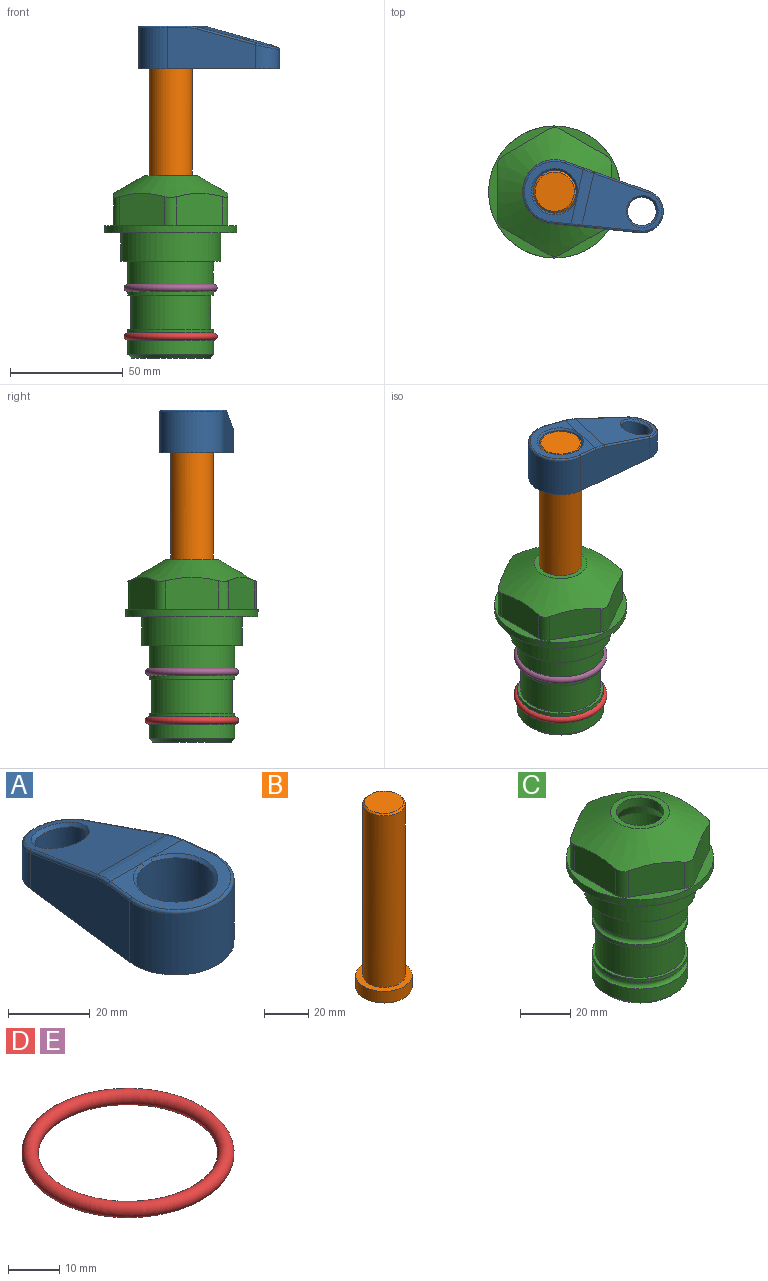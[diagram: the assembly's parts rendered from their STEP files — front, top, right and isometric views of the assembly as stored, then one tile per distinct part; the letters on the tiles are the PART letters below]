
ASSEMBLY  parts=5 mates=4
PART A: 31 faces, bbox 31.7x65.5x19.8 mm
  f0: plane 39.12x18.26mm, normal (0.99,0.12,0), area 612.2mm2, adj f1,f4,f7,f11,f13,f15
  f1: cylinder r=9.53mm len=18.91mm, axis (0,0,-1), area 296.1mm2, adj f0,f2,f7,f17
  f2: plane 39.12x18.26mm, normal (-0.99,0.12,0), area 612.2mm2, adj f1,f4,f7,f12,f14,f16
  f3: cylinder r=6.35mm len=12.7mm, axis (0,0,-1), area 362.4mm2, adj f7,f18
  f4: cylinder r=14.29mm len=28.58mm, axis (0,0,-1), area 882.2mm2, adj f0,f2,f7,f10
  f5: cylinder r=9.53mm len=19.05mm, axis (0,0,-1), area 1092.6mm2, adj f7,f19,f20
  f6: plane 26.99x23.69mm, normal (0,0,1), area 216.2mm2, adj f9,f10,f11,f12,f19
  f7: plane 63.5x28.58mm, normal (0,0,-1), area 661.8mm2, adj f0,f1,f2,f3,f4,f5,f22,f23
  f8: plane 33.52x23.6mm, normal (0,0.26,0.97), area 486mm2, adj f9,f15,f16,f17,f18
  f9: cylinder r=19.05mm len=24.72mm, axis (1,0,0), area 120.4mm2, adj f6,f8,f13,f14,f20
  f10: torus R=13.49mm, axis (0,0,1), area 59mm2, adj f4,f6,f11,f12
  f11: cylinder r=0.79mm len=8.67mm, axis (0.12,-0.99,0), area 10.8mm2, adj f0,f6,f10,f13
  f12: cylinder r=0.79mm len=8.67mm, axis (0.12,0.99,0), area 10.8mm2, adj f2,f6,f10,f14
  f13: bspline ~4.95x1.42mm, area 6.1mm2, adj f0,f9,f11,f15
  f14: bspline ~4.95x1.42mm, area 6.1mm2, adj f2,f9,f12,f16
  f15: cylinder r=0.79mm len=25.95mm, axis (0.12,-0.96,0.26), area 32.9mm2, adj f0,f8,f13,f17
  f16: cylinder r=0.79mm len=25.95mm, axis (0.12,0.96,-0.26), area 32.9mm2, adj f2,f8,f14,f17
  f17: bspline ~18.91x8.38mm, area 30mm2, adj f1,f8,f15,f16
  f18: bspline ~14.29x14.29mm, area 48.3mm2, adj f3,f8
  f19: cone r=9.53mm half-angle=45deg, axis (0,0,1), area 66.5mm2, adj f5,f6,f20
  f20: bspline ~3.22x0.96mm, area 3.5mm2, adj f5,f9,f19
  f21: plane 2.75x2.72mm, normal (0,0,-1), area 2.9mm2, adj f23,f25,f28
  f22: plane 23.05x15.88mm, normal (-0.99,-0.12,0), area 323.6mm2, adj f7,f25,f26,f27,f28,f29
  f23: plane 23.05x15.88mm, normal (0.99,-0.12,0), area 323.6mm2, adj f7,f21,f25,f27,f28,f30
  f24: cylinder r=9.53mm len=10.69mm, axis (0,0,-1), area 114.7mm2, adj f7,f27,f29,f30
  f25: cylinder r=12.7mm len=20.59mm, axis (0,0,-1), area 381.1mm2, adj f7,f21,f22,f23,f26,f28
  f26: plane 2.75x2.72mm, normal (0,0,-1), area 2.9mm2, adj f22,f25,f28
  f27: plane 19.72x18.37mm, normal (0,-0.26,-0.97), area 291.8mm2, adj f22,f23,f24,f28,f29,f30
  f28: cylinder r=15.88mm len=19.92mm, axis (1,0,0), area 54.8mm2, adj f21,f22,f23,f25,f26,f27
  f29: cylinder r=1.59mm len=11mm, axis (0,0,-1), area 34.7mm2, adj f7,f22,f24,f27
  f30: cylinder r=1.59mm len=11mm, axis (0,0,-1), area 34.7mm2, adj f7,f23,f24,f27
PART B: 6 faces, bbox 25.4x25.4x101.6 mm
  f0: plane 17.46x17.46mm, normal (0,0,1), area 239.5mm2, adj f5
  f1: plane 25.4x25.4mm, normal (0,0,-1), area 506.7mm2, adj f2
  f2: cylinder r=12.7mm len=25.4mm, axis (0,0,1), area 506.7mm2, adj f1,f3
  f3: plane 25.4x25.4mm, normal (0,0,1), area 221.7mm2, adj f2,f4
  f4: cylinder r=9.53mm len=94.46mm, axis (0,0,1), area 5653mm2, adj f3,f5
  f5: cone r=8.73mm half-angle=45deg, axis (0,0,-1), area 64.4mm2, adj f0,f4
PART C: 36 faces, bbox 58.7x58.7x81 mm
  f0: cylinder r=17.78mm len=35.56mm, axis (0,0,1), area 1670.8mm2, adj f23,f24,f31
  f1: cylinder r=19.05mm len=38.1mm, axis (0,0,1), area 1191.9mm2, adj f26,f27,f30
  f2: plane 58.66x58.66mm, normal (0,0,-1), area 1150.6mm2, adj f3,f28
  f3: cylinder r=29.33mm len=58.66mm, axis (0,0,-1), area 585.1mm2, adj f2,f4
  f4: plane 58.66x58.66mm, normal (0,0,1), area 475.9mm2, adj f3,f5,f6,f7,f8,f9,f10,f11
  f5: plane 20.32x14.34mm, normal (-0.5,0.87,0), area 324.4mm2, adj f4,f15,f16,f17
  f6: plane 20.32x14.34mm, normal (0.5,0.87,0), area 324.4mm2, adj f4,f14,f15,f17
  f7: plane 23.48x14.34mm, normal (1,0,0), area 324.4mm2, adj f4,f13,f14,f17
  f8: plane 20.32x14.34mm, normal (0.5,-0.87,0), area 324.4mm2, adj f4,f12,f13,f17
  f9: plane 20.32x14.34mm, normal (-0.5,-0.87,0), area 324.4mm2, adj f4,f11,f12,f17
  f10: plane 23.48x14.34mm, normal (-1,0,0), area 324.4mm2, adj f4,f11,f16,f17
  f11: cylinder r=5.08mm len=12.85mm, axis (0,0,-1), area 67.2mm2, adj f4,f9,f10,f17
  f12: cylinder r=5.08mm len=12.85mm, axis (0,0,-1), area 67.2mm2, adj f4,f8,f9,f17
  f13: cylinder r=5.08mm len=12.85mm, axis (0,0,-1), area 67.2mm2, adj f4,f7,f8,f17
  f14: cylinder r=5.08mm len=12.85mm, axis (0,0,-1), area 67.2mm2, adj f4,f6,f7,f17
  f15: cylinder r=5.08mm len=12.85mm, axis (0,0,-1), area 67.2mm2, adj f4,f5,f6,f17
  f16: cylinder r=5.08mm len=12.85mm, axis (0,0,-1), area 67.2mm2, adj f4,f5,f10,f17
  f17: cone r=11.73mm half-angle=60deg, axis (0,0,-1), area 2071.8mm2, adj f5,f6,f7,f8,f9,f10,f11,f12
  f18: plane 23.46x23.46mm, normal (0,0,1), area 147.4mm2, adj f17,f35
  f19: plane 34.93x34.93mm, normal (0,0,-1), area 958mm2, adj f29
  f20: cylinder r=19.05mm len=38.1mm, axis (0,0,1), area 760.1mm2, adj f21,f29
  f21: torus R=19.05mm, axis (0,0,1), area 565.3mm2, adj f20,f22
  f22: cylinder r=19.05mm len=38.1mm, axis (0,0,1), area 190mm2, adj f21,f23
  f23: plane 38.1x38.1mm, normal (0,0,1), area 146.9mm2, adj f0,f22
  f24: plane 38.1x38.1mm, normal (0,0,-1), area 146.9mm2, adj f0,f25
  f25: cylinder r=19.05mm len=38.1mm, axis (0,0,1), area 190mm2, adj f24,f26
  f26: torus R=19.05mm, axis (0,0,1), area 565.3mm2, adj f1,f25
  f27: plane 44.45x44.45mm, normal (0,0,-1), area 411.7mm2, adj f1,f28
  f28: cylinder r=22.23mm len=44.45mm, axis (0,0,1), area 1773.5mm2, adj f2,f27
  f29: cone r=19.05mm half-angle=45deg, axis (0,0,1), area 257.5mm2, adj f19,f20
  f30: cylinder r=3.17mm len=6.75mm, axis (-1,0,0), area 128mm2, adj f1,f33
  f31: cylinder r=3.17mm len=6.35mm, axis (-1,0,0), area 102.5mm2, adj f0,f33
  f32: plane 25.4x25.4mm, normal (0,0,1), area 506.7mm2, adj f33
  f33: cylinder r=12.7mm len=66.42mm, axis (0,0,-1), area 5236.2mm2, adj f30,f31,f32,f34
  f34: cone r=9.53mm half-angle=30deg, axis (0,0,-1), area 443.4mm2, adj f33,f35
  f35: cylinder r=9.53mm len=19.05mm, axis (0,0,-1), area 240.9mm2, adj f18,f34
PART D: 1 faces, bbox 44.7x44.7x3.2 mm
  f0: torus R=19.05mm, axis (0,0,1), area 1193.9mm2
PART E: same geometry as D
PLACE A rot(axis=(0,0,-1),102.7deg) t=(0,0,28.35)mm
PLACE B rot(axis=(0,0,-1),102.7deg) t=(0,0,27.55)mm
PLACE C at identity fixed
PLACE D t=(0,0,-21.59)mm
PLACE E at identity
MATE fastened E.f0 <-> C.f0  axis (0,0,1) through (0,0,-24.51)mm
MATE fastened A.f4 <-> B.f2  axis (0,0,-1) through (0,0,91.05)mm
MATE cylindrical B.f2 <-> C.f0  axis (0,0,-1) through (0,0,-10.55)mm
MATE fastened D.f0 <-> C.f0  axis (0,0,1) through (0,0,-46.1)mm
